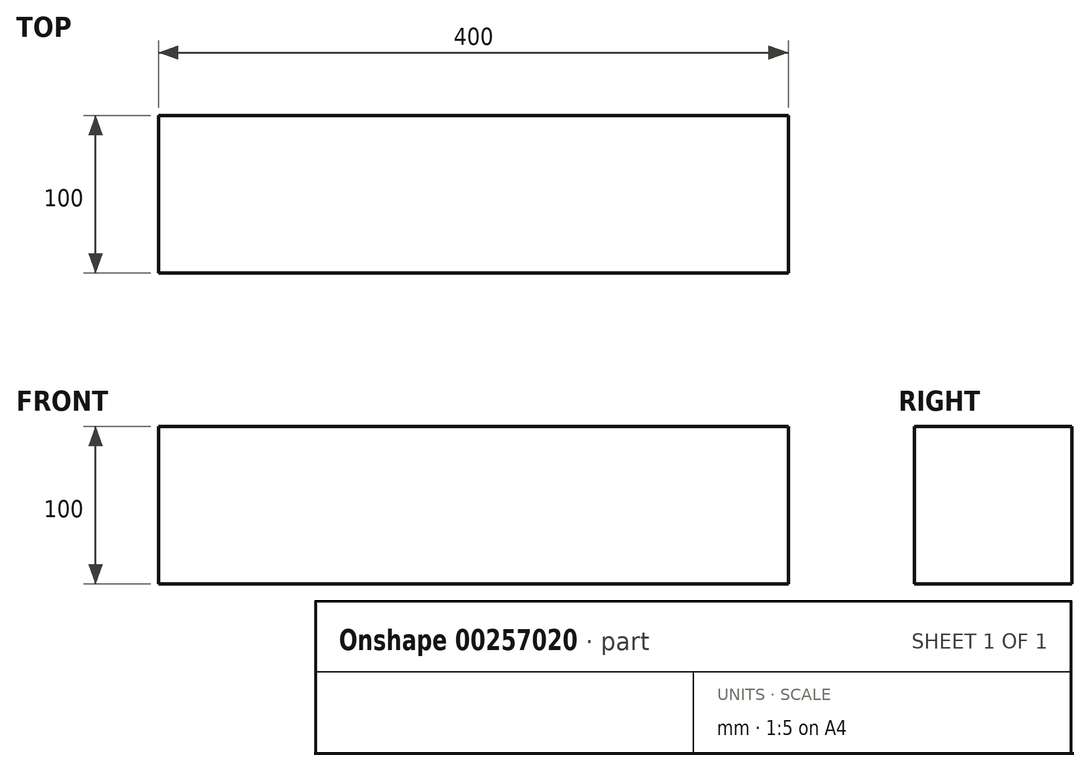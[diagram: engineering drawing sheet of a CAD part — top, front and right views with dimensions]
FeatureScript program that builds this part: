
annotation { "Feature Type Name" : "Feature", "Feature Type Description" : "" }
export const myFeature = defineFeature(function(context is Context, id is Id, definition is map)
    precondition{}
    {
        {
            var Q0;
            Q0=qCreatedBy(makeId("Top.planeOp"),FACE);
            var sketch = newSketch(context, id + "F0", { "sketchPlane" : qUnion([Q0])});
            skLineSegment(sketch, "E0.bottom", {"start": v(200, 50) * mm, "end": v(-200, 50) * mm});
            skLineSegment(sketch, "E0.top", {"start": v(200, -50) * mm, "end": v(-200, -50) * mm});
            skLineSegment(sketch, "E0.left", {"start": v(200, 50) * mm, "end": v(200, -50) * mm});
            skLineSegment(sketch, "E0.right", {"start": v(-200, 50) * mm, "end": v(-200, -50) * mm});
            skPoint(sketch, "E0.middle", {"position": v(0, 0) * mm});
            skSolve(sketch);
        }
        {
            var Q0;
            Q0 = qSketchRegion(id + "F0", true);
            extrude(context, id + "F1", {"entities" : qUnion([Q0]), "depth" : 100 * mm});
        }
    });
